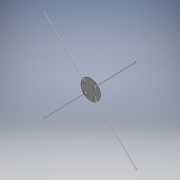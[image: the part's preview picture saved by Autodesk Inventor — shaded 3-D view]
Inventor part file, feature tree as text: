
AUTODESK INVENTOR PART (.ipt)
format: ipt  version: 2016 (Build 200138000, 138)  size: 126,464 bytes
history: native  units: mm
features: extrude x3, sketch x3, pattern_circular x1
ambient origin geometry x8: Origin, YZ Plane, XZ Plane, XY Plane, X Axis, Y Axis, Z Axis, Center Point
bodies: Solid1 (feature_tree)
feature tree (7):
  extrude  "Extrusion1"  Depth=1.0mm TaperAngle=0.0deg
  extrude  "Extrusion2"  Depth=10.0mm
  extrude  "Extrusion3"  Depth=418.75mm TaperAngle=360.0deg
  pattern_circular  "Circular Pattern1"  [2 undecoded]
  sketch  "Sketch1"  dims[d0=140.0mm d1=1.0mm d2=0.0mm]
  sketch  "Sketch2"  dims[d3=10.0mm d4=0.0mm d5=5.0mm]
  sketch  "Sketch3"  dims[d6=418.75mm d7=0.0mm d8=40.0mm d9=360.0deg]
note: 2 required parameter values undecoded (feature->parameter linkage not recoverable at this tier; creation-order binding heuristic only, values carry confidence <= 0.55)
